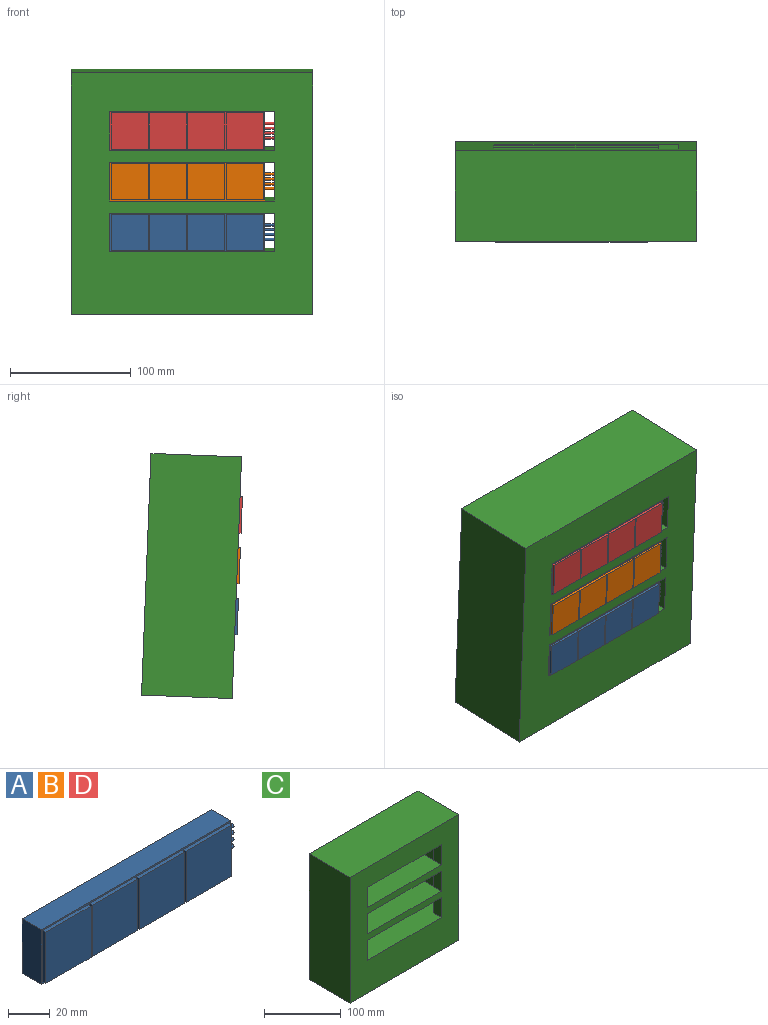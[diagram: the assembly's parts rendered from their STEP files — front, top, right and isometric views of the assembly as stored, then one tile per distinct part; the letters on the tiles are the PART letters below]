
ASSEMBLY  parts=4 mates=6
PART A: 34 faces, bbox 136x15x32 mm
  f0: plane 128x32mm, normal (0,-1,0), area 406mm2, adj f1,f2,f3,f4,f14,f15,f16,f17
  f1: plane 32x13mm, normal (1,0,0), area 403.4mm2, adj f0,f2,f4,f5,f6,f8,f10,f12
  f2: plane 128x13mm, normal (0,0,1), area 1664mm2, adj f0,f1,f3,f5
  f3: plane 32x13mm, normal (-1,0,0), area 416mm2, adj f0,f2,f4,f5
  f4: plane 128x13mm, normal (0,0,-1), area 1664mm2, adj f0,f1,f3,f5
  f5: plane 128x32mm, normal (0,1,0), area 4096mm2, adj f1,f2,f3,f4
  f6: cylinder r=1mm len=8mm, axis (-1,0,0), area 50.3mm2, adj f1,f7
  f7: plane 2x2mm, normal (1,0,0), area 3.1mm2, adj f6
  f8: cylinder r=1mm len=8mm, axis (-1,0,0), area 50.3mm2, adj f1,f9
  f9: plane 2x2mm, normal (1,0,0), area 3.1mm2, adj f8
  f10: cylinder r=1mm len=8mm, axis (-1,0,0), area 50.3mm2, adj f1,f11
  f11: plane 2x2mm, normal (1,0,0), area 3.1mm2, adj f10
  f12: cylinder r=1mm len=8mm, axis (-1,0,0), area 50.3mm2, adj f1,f13
  f13: plane 2x2mm, normal (1,0,0), area 3.1mm2, adj f12
  f14: plane 30x2mm, normal (1,0,0), area 60mm2, adj f0,f15,f17,f18
  f15: plane 30.75x2mm, normal (0,0,1), area 61.5mm2, adj f0,f14,f16,f18
  f16: plane 30x2mm, normal (-1,0,0), area 60mm2, adj f0,f15,f17,f18
  f17: plane 30.75x2mm, normal (0,0,-1), area 61.5mm2, adj f0,f14,f16,f18
  f18: plane 30.75x30mm, normal (0,-1,0), area 922.5mm2, adj f14,f15,f16,f17
  f19: plane 30x2mm, normal (1,0,0), area 60mm2, adj f0,f20,f22,f23
  f20: plane 30.75x2mm, normal (0,0,1), area 61.5mm2, adj f0,f19,f21,f23
  f21: plane 30x2mm, normal (-1,0,0), area 60mm2, adj f0,f20,f22,f23
  f22: plane 30.75x2mm, normal (0,0,-1), area 61.5mm2, adj f0,f19,f21,f23
  f23: plane 30.75x30mm, normal (0,-1,0), area 922.5mm2, adj f19,f20,f21,f22
  f24: plane 30x2mm, normal (1,0,0), area 60mm2, adj f0,f25,f27,f28
  f25: plane 30.75x2mm, normal (0,0,1), area 61.5mm2, adj f0,f24,f26,f28
  f26: plane 30x2mm, normal (-1,0,0), area 60mm2, adj f0,f25,f27,f28
  f27: plane 30.75x2mm, normal (0,0,-1), area 61.5mm2, adj f0,f24,f26,f28
  f28: plane 30.75x30mm, normal (0,-1,0), area 922.5mm2, adj f24,f25,f26,f27
  f29: plane 30x2mm, normal (1,0,0), area 60mm2, adj f0,f30,f32,f33
  f30: plane 30.75x2mm, normal (0,0,1), area 61.5mm2, adj f0,f29,f31,f33
  f31: plane 30x2mm, normal (-1,0,0), area 60mm2, adj f0,f30,f32,f33
  f32: plane 30.75x2mm, normal (0,0,-1), area 61.5mm2, adj f0,f29,f31,f33
  f33: plane 30.75x30mm, normal (0,-1,0), area 922.5mm2, adj f29,f30,f31,f32
PART B: same geometry as A
PART C: 25 faces, bbox 200x75x200 mm
  f0: plane 116x60mm, normal (-1,0,0), area 6960mm2, adj f2,f6,f14,f21
  f1: plane 32x15mm, normal (-1,0,0), area 480mm2, adj f2,f13,f19,f21
  f2: plane 116x17mm, normal (0,1,0), area 1972mm2, adj f0,f1,f4,f6,f7,f17,f20,f21
  f3: plane 75x32mm, normal (1,0,0), area 2400mm2, adj f13,f14,f19,f21
  f4: plane 32x15mm, normal (-1,0,0), area 480mm2, adj f2,f13,f16,f18
  f5: plane 75x32mm, normal (1,0,0), area 2400mm2, adj f13,f14,f16,f18
  f6: plane 153x75mm, normal (0,0,-1), area 11148.1mm2, adj f0,f2,f7,f12,f13,f14,f24
  f7: plane 32x15mm, normal (-1,0,0), area 480mm2, adj f2,f6,f13,f15
  f8: plane 200x75mm, normal (1,0,0), area 15000mm2, adj f9,f11,f13,f14
  f9: plane 200x75mm, normal (0,0,1), area 15000mm2, adj f8,f10,f13,f14
  f10: plane 200x75mm, normal (-1,0,0), area 15000mm2, adj f9,f11,f13,f14
  f11: plane 200x75mm, normal (0,0,-1), area 15000mm2, adj f8,f10,f13,f14
  f12: plane 75x32mm, normal (1,0,0), area 2400mm2, adj f6,f13,f14,f15
  f13: plane 200x200mm, normal (0,-1,0), area 26944mm2, adj f1,f3,f4,f5,f6,f7,f8,f9
  f14: plane 200x200mm, normal (0,1,0), area 24972mm2, adj f0,f3,f5,f6,f8,f9,f10,f11
  f15: plane 136x75mm, normal (0,0,1), area 10128.1mm2, adj f7,f12,f13,f14,f17,f24
  f16: plane 136x75mm, normal (0,0,-1), area 10128.1mm2, adj f4,f5,f13,f14,f17,f23
  f17: plane 60x10mm, normal (1,0,0), area 600mm2, adj f2,f14,f15,f16
  f18: plane 136x75mm, normal (0,0,1), area 10128.1mm2, adj f4,f5,f13,f14,f20,f23
  f19: plane 136x75mm, normal (0,0,-1), area 10128.1mm2, adj f1,f3,f13,f14,f20,f22
  f20: plane 60x10mm, normal (1,0,0), area 600mm2, adj f2,f14,f18,f19
  f21: plane 153x75mm, normal (0,0,1), area 11148.1mm2, adj f0,f1,f2,f3,f13,f14,f22
  f22: cylinder r=4.78mm len=32mm, axis (0,0,1), area 961.9mm2, adj f19,f21
  f23: cylinder r=4.78mm len=32mm, axis (0,0,1), area 961.9mm2, adj f16,f18
  f24: cylinder r=4.78mm len=32mm, axis (0,0,1), area 961.9mm2, adj f6,f15
PART D: same geometry as A
PLACE A rot(axis=(1,0,0),2.2deg) t=(-101.28,-161.77,-228)mm
PLACE B rot(axis=(1,0,0),2.2deg) t=(-101.28,-163.41,-186.03)mm
PLACE C rot(axis=(1,0,0),2.2deg) t=(-97.28,-101.07,-193.6)mm
PLACE D rot(axis=(1,0,0),2.2deg) t=(-101.28,-165.05,-144.06)mm
MATE planar B.f0 <-> C.f13  axis (0,-1,-0.04) through (-165.28,-177.02,-170.55)mm
MATE parallel D.f18 <-> C.f13  axis (0,-1,-0.04) through (-148.9,-180.04,-144.65)mm
MATE slider D.f3 <-> C.f12  axis (-1,0,0) through (-165.28,-171.54,-144.32)mm
MATE slider D.f2 <-> C.f6  axis (0,-0.04,1) through (-101.28,-172.17,-128.33)mm
MATE planar A.f0 <-> C.f13  axis (0,-1,-0.04) through (-165.28,-175.39,-212.52)mm
MATE planar D.f0 <-> C.f13  axis (0,-1,-0.04) through (-165.28,-178.66,-128.58)mm
